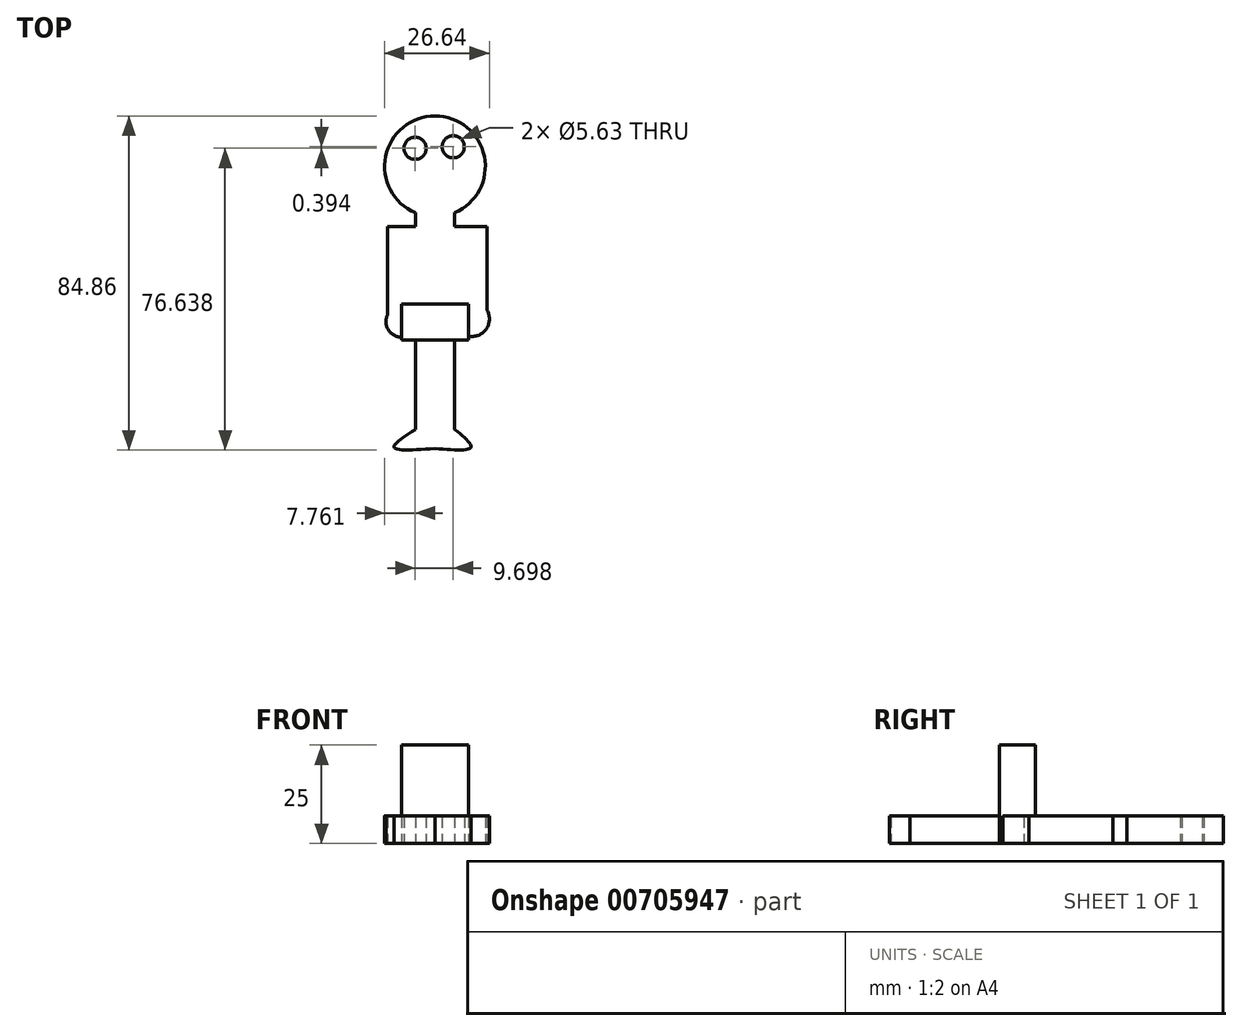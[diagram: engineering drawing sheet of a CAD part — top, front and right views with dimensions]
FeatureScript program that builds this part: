
annotation { "Feature Type Name" : "Feature", "Feature Type Description" : "" }
export const myFeature = defineFeature(function(context is Context, id is Id, definition is map)
    precondition{}
    {
        {
            var Q0;
            Q0=qCreatedBy(makeId("Top.planeOp"),FACE);
            var sketch = newSketch(context, id + "F0", { "sketchPlane" : qUnion([Q0])});
            skCircle(sketch, "E0", {"center": v(0, 27.64) * mm, "radius": 12.8 * mm});
            skLineSegment(sketch, "E1.bottom", {"start": v(4.97, 15.84) * mm, "end": v(5.04, 15.84) * mm});
            skLineSegment(sketch, "E1.top", {"start": v(-4.97, -19.4) * mm, "end": v(5.04, -19.4) * mm});
            skLineSegment(sketch, "E1.left", {"start": v(-4.97, 15.84) * mm, "end": v(-4.97, -19.4) * mm});
            skLineSegment(sketch, "E1.right", {"start": v(5.04, 15.84) * mm, "end": v(5.04, -19.4) * mm});
            skLineSegment(sketch, "E2", {"start": v(-4.97, 12.37) * mm, "end": v(-12.06, 12.37) * mm});
            skLineSegment(sketch, "E3", {"start": v(5.04, 12.37) * mm, "end": v(13.28, 12.37) * mm});
            skLineSegment(sketch, "E4", {"start": v(-12.06, 12.37) * mm, "end": v(-12.06, -10.23) * mm});
            skLineSegment(sketch, "E5", {"start": v(13.28, 12.37) * mm, "end": v(13.28, -9) * mm});
            skArc(sketch, "E6", {"start": v(-12.06, -10.23) * mm, "mid": v(-10.1, -15.41) * mm, "end": v(-4.97, -13.28) * mm});
            skCircle(sketch, "E7", {"center": v(-5.04, 32.22) * mm, "radius": 2.82 * mm});
            skCircle(sketch, "E8", {"center": v(4.66, 32.61) * mm, "radius": 2.82 * mm});
            skArc(sketch, "E9", {"start": v(5.04, -11.87) * mm, "mid": v(10.86, -15.34) * mm, "end": v(13.28, -9) * mm});
            skLineSegment(sketch, "E10", {"start": v(-4.97, -19.4) * mm, "end": v(-4.97, -39.22) * mm});
            skLineSegment(sketch, "E11", {"start": v(-4.97, -39.22) * mm, "end": v(0, -39.22) * mm});
            skLineSegment(sketch, "E12", {"start": v(0, -39.22) * mm, "end": v(0, -19.4) * mm});
            skLineSegment(sketch, "E13", {"start": v(5.04, -19.4) * mm, "end": v(5.04, -39.22) * mm});
            skLineSegment(sketch, "E14", {"start": v(5.04, -39.22) * mm, "end": v(0, -39.22) * mm});
            skFitSpline(sketch, "E15", {"points": [v(-4.97, -39.22) * mm, v(-10.37, -43.73) * mm, v(0, -44.03) * mm], "startDerivative": vector(-18.93, -12.11) * mm, "endDerivative": vector(27.37, 2.04) * mm});
            skLineSegment(sketch, "E16", {"start": v(0, -39.22) * mm, "end": v(0, -44.03) * mm});
            skFitSpline(sketch, "E17", {"points": [v(5.04, -39.22) * mm, v(9.17, -43.73) * mm, v(0, -44.03) * mm], "startDerivative": vector(15, -12.16) * mm, "endDerivative": vector(-23.76, 2.07) * mm});
            skSolve(sketch);
        }
        {
            var Q0;
            {var subQ6=sQuery(id+"F0.wireOp",EDGE,"E1.bottom");Q0=makeQuery(id+"F0.imprint","IMPRINT",FACE,{"disambiguationData":[TD([[makeQuery(id+"F0.imprint","IMPRINT",EDGE,{"derivedFrom":subQ6}),-1.0]])]});}
            var Q1;
            {var subQ0=sQuery(id+"F0.wireOp",EDGE,"E3");Q1=makeQuery(id+"F0.imprint","IMPRINT",FACE,{"disambiguationData":[TD([[makeQuery(id+"F0.imprint","IMPRINT",EDGE,{"derivedFrom":subQ0}),-1.0]])]});}
            var Q2;
            {var subQ0=sQuery(id+"F0.wireOp",EDGE,"E2");Q2=makeQuery(id+"F0.imprint","IMPRINT",FACE,{"disambiguationData":[TD([[makeQuery(id+"F0.imprint","IMPRINT",EDGE,{"derivedFrom":subQ0}),1.0]])]});}
            var Q3;
            Q3=makeQuery(id+"F0.imprint","IMPRINT",FACE,{"disambiguationData":[TD([[makeQuery(id+"F0.imprint","IMPRINT",EDGE,{"derivedFrom":sQuery(id+"F0.wireOp",EDGE,"E14")}),1.0]])]});
            var Q4;
            {var subQ2=sQuery(id+"F0.wireOp",EDGE,"E12");Q4=makeQuery(id+"F0.imprint","IMPRINT",FACE,{"disambiguationData":[TD([[makeQuery(id+"F0.imprint","IMPRINT",EDGE,{"derivedFrom":subQ2}),-1.0]])]});}
            var Q5;
            Q5=makeQuery(id+"F0.imprint","IMPRINT",FACE,{"disambiguationData":[TD([[makeQuery(id+"F0.imprint","IMPRINT",EDGE,{"derivedFrom":sQuery(id+"F0.wireOp",EDGE,"E7")}),-1.0]])]});
            var Q6;
            Q6=makeQuery(id+"F0.imprint","IMPRINT",FACE,{"disambiguationData":[TD([[makeQuery(id+"F0.imprint","IMPRINT",EDGE,{"derivedFrom":sQuery(id+"F0.wireOp",EDGE,"E11")}),-1.0]])]});
            var Q7;
            {var subQ0=sQuery(id+"F0.wireOp",EDGE,"E10");Q7=makeQuery(id+"F0.imprint","IMPRINT",FACE,{"disambiguationData":[TD([[makeQuery(id+"F0.imprint","IMPRINT",EDGE,{"derivedFrom":subQ0}),1.0]])]});}
            extrude(context, id + "F1", {"entities" : qUnion([Q0, Q1, Q2, Q3, Q4, Q5, Q6, Q7]), "depth" : 7 * mm, "offsetDistance" : 25 * mm});
        }
        {
            var Q0;
            Q0=qCreatedBy(makeId("Top.planeOp"),FACE);
            var sketch = newSketch(context, id + "F2", { "sketchPlane" : qUnion([Q0])});
            skLineSegment(sketch, "E18.bottom", {"start": v(8.52, -7.33) * mm, "end": v(-8.52, -7.33) * mm});
            skLineSegment(sketch, "E18.top", {"start": v(8.52, -16.53) * mm, "end": v(-8.52, -16.53) * mm});
            skLineSegment(sketch, "E18.left", {"start": v(8.52, -7.33) * mm, "end": v(8.52, -16.53) * mm});
            skLineSegment(sketch, "E18.right", {"start": v(-8.52, -7.33) * mm, "end": v(-8.52, -16.53) * mm});
            skSolve(sketch);
        }
        {
            var Q0;
            Q0=makeQuery(id+"F2.imprint","IMPRINT",FACE,{"disambiguationData":[TD([[makeQuery(id+"F2.imprint","IMPRINT",EDGE,{"derivedFrom":sQuery(id+"F2.wireOp",EDGE,"E18.bottom")}),1.0]])]});
            extrude(context, id + "F3", {"entities" : qUnion([Q0]), "operationType" : NewBodyOperationType.ADD, "depth" : 25 * mm, "offsetDistance" : 25 * mm});
        }
    });
